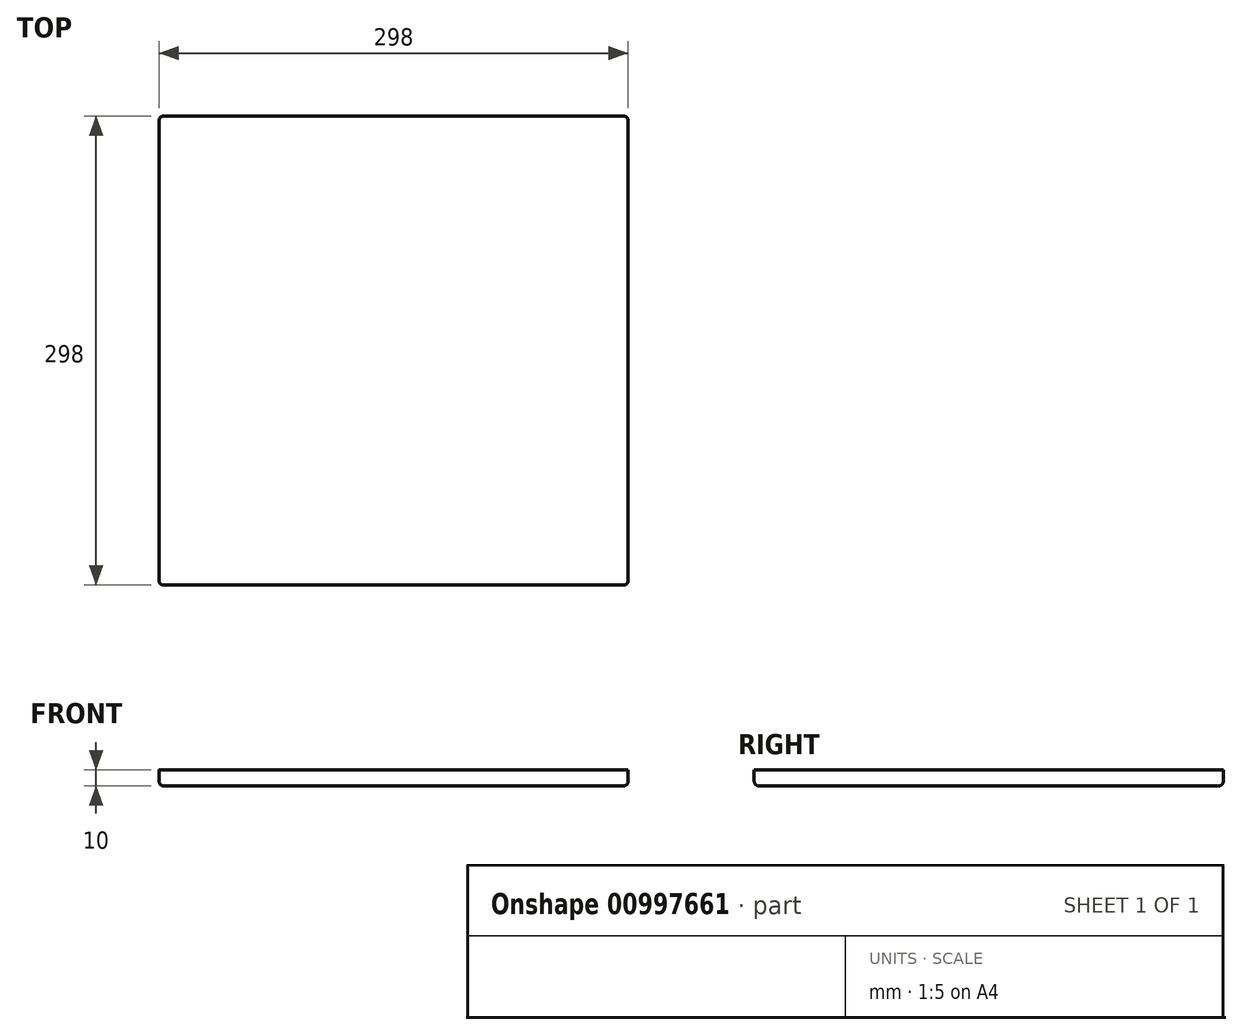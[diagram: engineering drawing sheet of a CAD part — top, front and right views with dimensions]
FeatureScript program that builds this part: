
annotation { "Feature Type Name" : "Feature", "Feature Type Description" : "" }
export const myFeature = defineFeature(function(context is Context, id is Id, definition is map)
    precondition{}
    {
        {
            var Q0;
            Q0=qCreatedBy(makeId("Top.planeOp"),FACE);
            var sketch = newSketch(context, id + "F0", { "sketchPlane" : qUnion([Q0])});
            skLineSegment(sketch, "E0.bottom", {"start": v(-155.75, 125.21) * mm, "end": v(142.25, 125.21) * mm});
            skLineSegment(sketch, "E0.top", {"start": v(-155.75, -172.79) * mm, "end": v(142.25, -172.79) * mm});
            skLineSegment(sketch, "E0.left", {"start": v(-155.75, 125.21) * mm, "end": v(-155.75, -172.79) * mm});
            skLineSegment(sketch, "E0.right", {"start": v(142.25, 125.21) * mm, "end": v(142.25, -172.79) * mm});
            skSolve(sketch);
        }
        {
            var Q0;
            Q0=makeQuery(id+"F0.imprint","IMPRINT",FACE,{"disambiguationData":[TD([[makeQuery(id+"F0.imprint","IMPRINT",EDGE,{"derivedFrom":sQuery(id+"F0.wireOp",EDGE,"E0.bottom")}),-1.0]])]});
            extrude(context, id + "F1", {"entities" : qUnion([Q0]), "depth" : 10 * mm, "offsetDistance" : 25 * mm});
        }
        {
            var Q0;
            Q0=makeQuery(id+"F1.opExtrude","SWEPT_EDGE",EDGE,{"disambiguationData":[OSD([sQuery(id+"F0.wireOp",EDGE,"E0.top"),sQuery(id+"F0.wireOp",EDGE,"E0.left")])]});
            var Q1;
            Q1=makeQuery(id+"F1.opExtrude","SWEPT_EDGE",EDGE,{"disambiguationData":[OSD([sQuery(id+"F0.wireOp",EDGE,"E0.top"),sQuery(id+"F0.wireOp",EDGE,"E0.right")])]});
            var Q2;
            Q2=makeQuery(id+"F1.opExtrude","SWEPT_EDGE",EDGE,{"disambiguationData":[OSD([sQuery(id+"F0.wireOp",EDGE,"E0.bottom"),sQuery(id+"F0.wireOp",EDGE,"E0.right")])]});
            var Q3;
            Q3=makeQuery(id+"F1.opExtrude","CAP_EDGE",EDGE,{"disambiguationData":[OSD([sQuery(id+"F0.wireOp",EDGE,"E0.right")])],"isStart":true});
            var Q4;
            Q4=makeQuery(id+"F1.opExtrude","CAP_EDGE",EDGE,{"disambiguationData":[OSD([sQuery(id+"F0.wireOp",EDGE,"E0.top")])],"isStart":true});
            var Q5;
            Q5=makeQuery(id+"F1.opExtrude","SWEPT_EDGE",EDGE,{"disambiguationData":[OSD([sQuery(id+"F0.wireOp",EDGE,"E0.bottom"),sQuery(id+"F0.wireOp",EDGE,"E0.left")])]});
            var Q6;
            Q6=makeQuery(id+"F1.opExtrude","CAP_EDGE",EDGE,{"disambiguationData":[OSD([sQuery(id+"F0.wireOp",EDGE,"E0.left")])],"isStart":true});
            var Q7;
            Q7=makeQuery(id+"F1.opExtrude","CAP_EDGE",EDGE,{"disambiguationData":[OSD([sQuery(id+"F0.wireOp",EDGE,"E0.bottom")])],"isStart":true});
            fillet(context, id + "F2", {"entities" : qUnion([Q0, Q1, Q2, Q3, Q4, Q5, Q6, Q7]), "tangentPropagation" : true, "radius" : 3 * mm, "defaultsChanged" : false, "vertexSettings" : [], "allowEdgeOverflow" : false});
        }
    });
